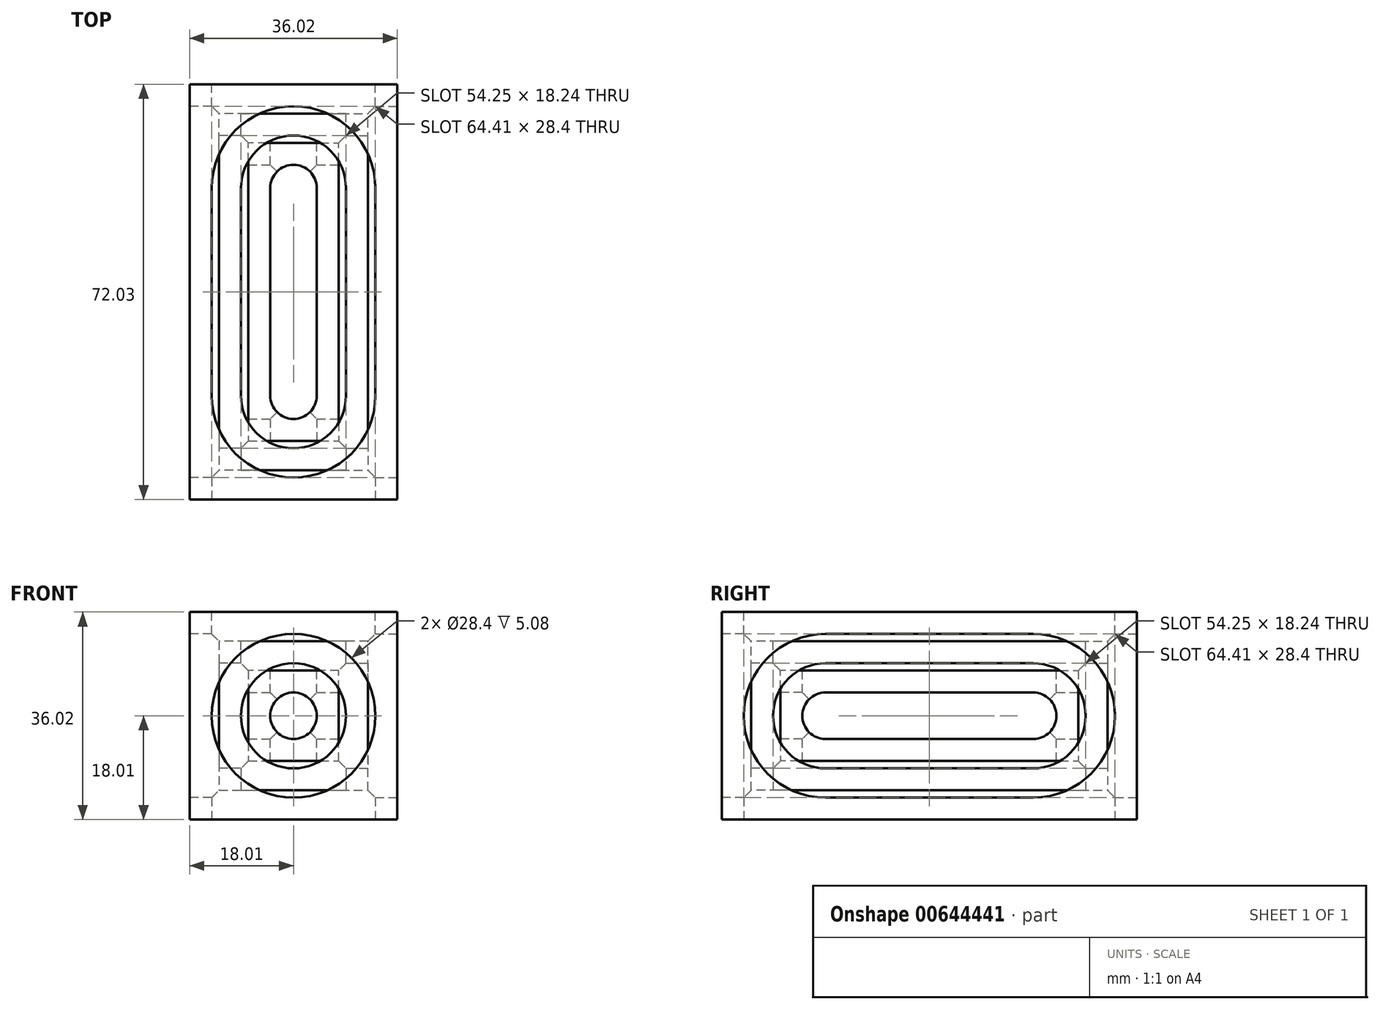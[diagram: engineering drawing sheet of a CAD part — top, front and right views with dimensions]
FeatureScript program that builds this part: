
annotation { "Feature Type Name" : "Feature", "Feature Type Description" : "" }
export const myFeature = defineFeature(function(context is Context, id is Id, definition is map)
    precondition{}
    {
        {
            var Q0;
            Q0=qCreatedBy(makeId("Front.planeOp"),FACE);
            var sketch = newSketch(context, id + "F0", { "sketchPlane" : qUnion([Q0])});
            skLineSegment(sketch, "E0.bottom", {"start": v(18, 18) * mm, "end": v(-18, 18) * mm});
            skLineSegment(sketch, "E0.top", {"start": v(18, -18) * mm, "end": v(-18, -18) * mm});
            skLineSegment(sketch, "E0.left", {"start": v(18, 18) * mm, "end": v(18, -18) * mm});
            skLineSegment(sketch, "E0.right", {"start": v(-18, 18) * mm, "end": v(-18, -18) * mm});
            skPoint(sketch, "E0.middle", {"position": v(0, 0) * mm});
            skSolve(sketch);
        }
        {
            var Q0;
            Q0 = qSketchRegion(id + "F0", true);
            extrude(context, id + "F1", {"entities" : qUnion([Q0]), "oppositeDirection" : true, "depth" : 72.03 * mm, "offsetDistance" : 25.4 * mm});
        }
        {
            var Q0;
            Q0=makeQuery(id+"F1.opExtrude","CAP_FACE",FACE,{"disambiguationData":[OSD([sQuery(id+"F0.wireOp",EDGE,"E0.bottom"),sQuery(id+"F0.wireOp",EDGE,"E0.top"),sQuery(id+"F0.wireOp",EDGE,"E0.left"),sQuery(id+"F0.wireOp",EDGE,"E0.right")])],"isStart":false});
            extrude(context, id + "F2", {"entities" : qUnion([Q0]), "depth" : 30.3 * mm, "offsetDistance" : 25.4 * mm});
        }
        {
            var Q0;
            Q0=makeQuery(id+"F1.opExtrude","SWEPT_FACE",FACE,{"disambiguationData":[OSD([sQuery(id+"F0.wireOp",EDGE,"E0.bottom")])]});
            var sketch = newSketch(context, id + "F3", { "sketchPlane" : qUnion([Q0])});
            skLineSegment(sketch, "E1", {"start": v(-18, 0) * mm, "end": v(-18, 36.02) * mm});
            skLineSegment(sketch, "E2", {"start": v(-18, 36.02) * mm, "end": v(-18, 72.03) * mm});
            skLineSegment(sketch, "E3", {"start": v(-18, 72.03) * mm, "end": v(0, 72.03) * mm});
            skLineSegment(sketch, "E4", {"start": v(0, 72.03) * mm, "end": v(0, 68.22) * mm});
            skLineSegment(sketch, "E5", {"start": v(-18, 0) * mm, "end": v(0, 0) * mm});
            skLineSegment(sketch, "E6", {"start": v(0, 0) * mm, "end": v(0, 3.81) * mm});
            skCircle(sketch, "E7", {"center": v(0, 18) * mm, "radius": 14.2 * mm});
            skPoint(sketch, "E7.centerSnap0", {"position": v(-18, 18) * mm});
            skCircle(sketch, "E8", {"center": v(0, 54.03) * mm, "radius": 14.2 * mm});
            skPoint(sketch, "E8.centerSnap0", {"position": v(-18, 54.03) * mm});
            skLineSegment(sketch, "E9", {"start": v(-14.2, 54.03) * mm, "end": v(-14.2, 18) * mm});
            skLineSegment(sketch, "E10", {"start": v(14.2, 54.03) * mm, "end": v(14.2, 18) * mm});
            skSolve(sketch);
        }
        {
            var Q0;
            {var subQ0=sQuery(id+"F3.wireOp",EDGE,"E7");var subQ1=makeQuery(id+"F3.imprint","INTERSECT",VERTEX,{"derivedFrom":[subQ0,sQuery(id+"F3.wireOp",EDGE,"E9")]});Q0=makeQuery(id+"F3.imprint","IMPRINT",FACE,{"disambiguationData":[TD([[makeQuery(id+"F3.imprint","IMPRINT",EDGE,{"disambiguationData":[TD([[subQ1,1.0]])],"derivedFrom":subQ0}),1.0]])]});}
            var Q1;
            {var subQ0=sQuery(id+"F3.wireOp",EDGE,"E8");var subQ1=makeQuery(id+"F3.imprint","INTERSECT",VERTEX,{"derivedFrom":[sQuery(id+"F3.wireOp",EDGE,"E4"),subQ0]});Q1=makeQuery(id+"F3.imprint","IMPRINT",FACE,{"disambiguationData":[TD([[makeQuery(id+"F3.imprint","IMPRINT",EDGE,{"disambiguationData":[TD([[subQ1,1.0]])],"derivedFrom":subQ0}),1.0]])]});}
            var Q2;
            {var subQ0=sQuery(id+"F3.wireOp",EDGE,"E9");Q2=makeQuery(id+"F3.imprint","IMPRINT",FACE,{"disambiguationData":[TD([[makeQuery(id+"F3.imprint","IMPRINT",EDGE,{"derivedFrom":subQ0}),1.0]])]});}
            extrude(context, id + "F4", {"entities" : qUnion([Q0, Q1, Q2]), "operationType" : NewBodyOperationType.REMOVE, "oppositeDirection" : true, "depth" : 5.08 * mm, "offsetDistance" : 25.4 * mm});
        }
        {
            var Q0;
            Q0=makeQuery(id+"F1.opExtrude","SWEPT_FACE",FACE,{"disambiguationData":[OSD([sQuery(id+"F0.wireOp",EDGE,"E0.left")])]});
            var sketch = newSketch(context, id + "F5", { "sketchPlane" : qUnion([Q0])});
            skLineSegment(sketch, "E11", {"start": v(0, 18) * mm, "end": v(36.02, 18) * mm});
            skLineSegment(sketch, "E12", {"start": v(36.02, 18) * mm, "end": v(72.03, 18) * mm});
            skLineSegment(sketch, "E13", {"start": v(72.03, 18) * mm, "end": v(72.03, 0) * mm});
            skLineSegment(sketch, "E14", {"start": v(72.03, 0) * mm, "end": v(68.22, 0) * mm});
            skLineSegment(sketch, "E15", {"start": v(0, 0) * mm, "end": v(3.81, 0) * mm});
            skCircle(sketch, "E16", {"center": v(18, 0) * mm, "radius": 14.2 * mm});
            skPoint(sketch, "E16.centerSnap0", {"position": v(18, 18) * mm});
            skCircle(sketch, "E17", {"center": v(54.03, 0) * mm, "radius": 14.2 * mm});
            skPoint(sketch, "E17.centerSnap0", {"position": v(54.03, 18) * mm});
            skLineSegment(sketch, "E18", {"start": v(18, 14.2) * mm, "end": v(54.03, 14.2) * mm});
            skLineSegment(sketch, "E19", {"start": v(18, -14.2) * mm, "end": v(54.03, -14.2) * mm});
            skSolve(sketch);
        }
        {
            var Q0;
            Q0 = qSketchRegion(id + "F5", true);
            extrude(context, id + "F6", {"entities" : qUnion([Q0]), "operationType" : NewBodyOperationType.REMOVE, "oppositeDirection" : true, "depth" : 5.08 * mm, "offsetDistance" : 25.4 * mm});
        }
        {
            var Q0;
            Q0=makeQuery(id+"F1.opExtrude","SWEPT_FACE",FACE,{"disambiguationData":[OSD([sQuery(id+"F0.wireOp",EDGE,"E0.top")])]});
            var sketch = newSketch(context, id + "F7", { "sketchPlane" : qUnion([Q0])});
            skLineSegment(sketch, "E20", {"start": v(18, 0) * mm, "end": v(18, -36.02) * mm});
            skLineSegment(sketch, "E21", {"start": v(18, -36.02) * mm, "end": v(18, -72.03) * mm});
            skLineSegment(sketch, "E22", {"start": v(18, -72.03) * mm, "end": v(0, -72.03) * mm});
            skLineSegment(sketch, "E23", {"start": v(0, -72.03) * mm, "end": v(0, -68.22) * mm});
            skLineSegment(sketch, "E24", {"start": v(0, 0) * mm, "end": v(0, -3.81) * mm});
            skCircle(sketch, "E25", {"center": v(0, -54.03) * mm, "radius": 14.2 * mm});
            skPoint(sketch, "E25.centerSnap0", {"position": v(18, -54.03) * mm});
            skCircle(sketch, "E26", {"center": v(0, -18) * mm, "radius": 14.2 * mm});
            skPoint(sketch, "E26.centerSnap0", {"position": v(18, -18) * mm});
            skLineSegment(sketch, "E27", {"start": v(-14.2, -18) * mm, "end": v(-14.2, -54.03) * mm});
            skLineSegment(sketch, "E28", {"start": v(14.2, -54.03) * mm, "end": v(14.2, -18) * mm});
            skSolve(sketch);
        }
        {
            var Q0;
            Q0 = qSketchRegion(id + "F7", true);
            extrude(context, id + "F8", {"entities" : qUnion([Q0]), "operationType" : NewBodyOperationType.REMOVE, "oppositeDirection" : true, "depth" : 5.08 * mm, "offsetDistance" : 25.4 * mm});
        }
        {
            var Q0;
            Q0=makeQuery(id+"F1.opExtrude","SWEPT_FACE",FACE,{"disambiguationData":[OSD([sQuery(id+"F0.wireOp",EDGE,"E0.right")])]});
            var sketch = newSketch(context, id + "F9", { "sketchPlane" : qUnion([Q0])});
            skLineSegment(sketch, "E29", {"start": v(0, 18) * mm, "end": v(-36.02, 18) * mm});
            skLineSegment(sketch, "E30", {"start": v(-36.02, 18) * mm, "end": v(-72.03, 18) * mm});
            skLineSegment(sketch, "E31", {"start": v(-72.03, 18) * mm, "end": v(-72.03, 0) * mm});
            skLineSegment(sketch, "E32", {"start": v(-72.03, 0) * mm, "end": v(-68.22, 0) * mm});
            skLineSegment(sketch, "E33", {"start": v(0, 0) * mm, "end": v(-3.81, 0) * mm});
            skCircle(sketch, "E34", {"center": v(-54.03, 0) * mm, "radius": 14.2 * mm});
            skPoint(sketch, "E34.centerSnap0", {"position": v(-54.03, 18) * mm});
            skCircle(sketch, "E35", {"center": v(-18, 0) * mm, "radius": 14.2 * mm});
            skPoint(sketch, "E35.centerSnap0", {"position": v(-18, 18) * mm});
            skLineSegment(sketch, "E36", {"start": v(-54.03, 14.2) * mm, "end": v(-18, 14.2) * mm});
            skLineSegment(sketch, "E37", {"start": v(-18, -14.2) * mm, "end": v(-54.03, -14.2) * mm});
            skSolve(sketch);
        }
        {
            var Q0;
            Q0 = qSketchRegion(id + "F9", true);
            extrude(context, id + "F10", {"entities" : qUnion([Q0]), "operationType" : NewBodyOperationType.REMOVE, "oppositeDirection" : true, "depth" : 5.08 * mm, "offsetDistance" : 25.4 * mm});
        }
        {
            var Q0;
            Q0=makeQuery(id+"F1.opExtrude","CAP_FACE",FACE,{"disambiguationData":[OSD([sQuery(id+"F0.wireOp",EDGE,"E0.bottom"),sQuery(id+"F0.wireOp",EDGE,"E0.top"),sQuery(id+"F0.wireOp",EDGE,"E0.left"),sQuery(id+"F0.wireOp",EDGE,"E0.right")])],"isStart":true});
            var sketch = newSketch(context, id + "F11", { "sketchPlane" : qUnion([Q0])});
            skLineSegment(sketch, "E38", {"start": v(-18, 0) * mm, "end": v(-18, 18) * mm});
            skLineSegment(sketch, "E39", {"start": v(-18, 18) * mm, "end": v(-18, 0) * mm});
            skLineSegment(sketch, "E40", {"start": v(-18, 0) * mm, "end": v(-14.2, 0) * mm});
            skCircle(sketch, "E41", {"center": v(0, 0) * mm, "radius": 14.2 * mm});
            skSolve(sketch);
        }
        {
            var Q0;
            Q0 = qSketchRegion(id + "F11", true);
            extrude(context, id + "F12", {"entities" : qUnion([Q0]), "operationType" : NewBodyOperationType.REMOVE, "oppositeDirection" : true, "depth" : 5.08 * mm, "offsetDistance" : 25.4 * mm});
        }
        {
            var Q0;
            Q0=makeQuery(id+"F12.boolean.opBoolean","COPY",FACE,{"derivedFrom":makeQuery(id+"F12.opExtrude","CAP_FACE",FACE,{"disambiguationData":[OSD([sQuery(id+"F11.wireOp",EDGE,"E41")])],"isStart":false})});
            var sketch = newSketch(context, id + "F13", { "sketchPlane" : qUnion([Q0])});
            skLineSegment(sketch, "E42", {"start": v(-5.87, 12.93) * mm, "end": v(0, 12.93) * mm});
            skLineSegment(sketch, "E43", {"start": v(0, 12.93) * mm, "end": v(0, 9.12) * mm});
            skCircle(sketch, "E44", {"center": v(0, 0) * mm, "radius": 9.12 * mm});
            skSolve(sketch);
        }
        {
            var Q0;
            Q0 = qSketchRegion(id + "F13", true);
            extrude(context, id + "F14", {"entities" : qUnion([Q0]), "operationType" : NewBodyOperationType.REMOVE, "oppositeDirection" : true, "depth" : 5.08 * mm, "offsetDistance" : 25.4 * mm});
        }
        {
            var Q0;
            Q0=makeQuery(id+"F1.opExtrude","CAP_FACE",FACE,{"disambiguationData":[OSD([sQuery(id+"F0.wireOp",EDGE,"E0.bottom"),sQuery(id+"F0.wireOp",EDGE,"E0.top"),sQuery(id+"F0.wireOp",EDGE,"E0.left"),sQuery(id+"F0.wireOp",EDGE,"E0.right")])],"isStart":false});
            var sketch = newSketch(context, id + "F15", { "sketchPlane" : qUnion([Q0])});
            skLineSegment(sketch, "E45", {"start": v(0, 18) * mm, "end": v(0, 14.2) * mm});
            skPoint(sketch, "E45.endSnap0", {"position": v(0, 18) * mm});
            skCircle(sketch, "E46", {"center": v(0, 0) * mm, "radius": 14.2 * mm});
            skSolve(sketch);
        }
        {
            var Q0;
            Q0 = qSketchRegion(id + "F15", true);
            extrude(context, id + "F16", {"entities" : qUnion([Q0]), "operationType" : NewBodyOperationType.REMOVE, "oppositeDirection" : true, "depth" : 5.08 * mm, "offsetDistance" : 25.4 * mm});
        }
        {
            var Q0;
            Q0=makeQuery(id+"F6.boolean.opBoolean","COPY",FACE,{"derivedFrom":makeQuery(id+"F6.opExtrude","CAP_FACE",FACE,{"disambiguationData":[OSD([sQuery(id+"F5.wireOp",EDGE,"E16"),sQuery(id+"F5.wireOp",EDGE,"E17"),sQuery(id+"F5.wireOp",EDGE,"E18"),sQuery(id+"F5.wireOp",EDGE,"E19")])],"isStart":false})});
            var sketch = newSketch(context, id + "F17", { "sketchPlane" : qUnion([Q0])});
            skLineSegment(sketch, "E47", {"start": v(5.08, 0) * mm, "end": v(8.9, 0) * mm});
            skPoint(sketch, "E47.endSnap0", {"position": v(5.08, 0) * mm});
            skLineSegment(sketch, "E48", {"start": v(66.95, 0) * mm, "end": v(63.14, 0) * mm});
            skCircle(sketch, "E49", {"center": v(18, 0) * mm, "radius": 9.12 * mm});
            skCircle(sketch, "E50", {"center": v(54.03, 0) * mm, "radius": 9.12 * mm});
            skLineSegment(sketch, "E51", {"start": v(18, 9.12) * mm, "end": v(54.03, 9.12) * mm});
            skLineSegment(sketch, "E52", {"start": v(18, -9.12) * mm, "end": v(54.03, -9.12) * mm});
            skSolve(sketch);
        }
        {
            var Q0;
            Q0 = qSketchRegion(id + "F17", true);
            extrude(context, id + "F18", {"entities" : qUnion([Q0]), "operationType" : NewBodyOperationType.REMOVE, "oppositeDirection" : true, "depth" : 5.08 * mm, "offsetDistance" : 25.4 * mm});
        }
        {
            var Q0;
            Q0=makeQuery(id+"F4.boolean.opBoolean","COPY",FACE,{"derivedFrom":makeQuery(id+"F4.opExtrude","CAP_FACE",FACE,{"disambiguationData":[OSD([sQuery(id+"F3.wireOp",EDGE,"E7"),sQuery(id+"F3.wireOp",EDGE,"E8"),sQuery(id+"F3.wireOp",EDGE,"E9"),sQuery(id+"F3.wireOp",EDGE,"E10")])],"isStart":false})});
            var sketch = newSketch(context, id + "F19", { "sketchPlane" : qUnion([Q0])});
            skLineSegment(sketch, "E53", {"start": v(0, 5.08) * mm, "end": v(0, 8.9) * mm});
            skPoint(sketch, "E53.endSnap0", {"position": v(0, 5.08) * mm});
            skLineSegment(sketch, "E54", {"start": v(0, 66.95) * mm, "end": v(0, 63.14) * mm});
            skPoint(sketch, "E54.endSnap0", {"position": v(0, 66.95) * mm});
            skCircle(sketch, "E55", {"center": v(0, 54.03) * mm, "radius": 9.12 * mm});
            skCircle(sketch, "E56", {"center": v(0, 18) * mm, "radius": 9.12 * mm});
            skLineSegment(sketch, "E57", {"start": v(-9.12, 54.03) * mm, "end": v(-9.12, 18) * mm});
            skLineSegment(sketch, "E58", {"start": v(9.12, 54.03) * mm, "end": v(9.12, 18) * mm});
            skSolve(sketch);
        }
        {
            var Q0;
            Q0 = qSketchRegion(id + "F19", true);
            extrude(context, id + "F20", {"entities" : qUnion([Q0]), "operationType" : NewBodyOperationType.REMOVE, "oppositeDirection" : true, "depth" : 5.08 * mm, "offsetDistance" : 25.4 * mm});
        }
        {
            var Q0;
            Q0=makeQuery(id+"F10.boolean.opBoolean","COPY",FACE,{"derivedFrom":makeQuery(id+"F10.opExtrude","CAP_FACE",FACE,{"disambiguationData":[OSD([sQuery(id+"F9.wireOp",EDGE,"E34"),sQuery(id+"F9.wireOp",EDGE,"E35"),sQuery(id+"F9.wireOp",EDGE,"E36"),sQuery(id+"F9.wireOp",EDGE,"E37")])],"isStart":false})});
            var sketch = newSketch(context, id + "F21", { "sketchPlane" : qUnion([Q0])});
            skLineSegment(sketch, "E59", {"start": v(-66.95, 0) * mm, "end": v(-63.14, 0) * mm});
            skPoint(sketch, "E59.endSnap0", {"position": v(-66.95, 0) * mm});
            skLineSegment(sketch, "E60", {"start": v(-5.08, 0) * mm, "end": v(-8.9, 0) * mm});
            skPoint(sketch, "E60.endSnap0", {"position": v(-5.08, 0) * mm});
            skCircle(sketch, "E61", {"center": v(-54.03, 0) * mm, "radius": 9.12 * mm});
            skCircle(sketch, "E62", {"center": v(-18, 0) * mm, "radius": 9.12 * mm});
            skLineSegment(sketch, "E63", {"start": v(-54.03, 9.12) * mm, "end": v(-18, 9.12) * mm});
            skLineSegment(sketch, "E64", {"start": v(-18, -9.12) * mm, "end": v(-54.03, -9.12) * mm});
            skSolve(sketch);
        }
        {
            var Q0;
            Q0 = qSketchRegion(id + "F21", true);
            extrude(context, id + "F22", {"entities" : qUnion([Q0]), "operationType" : NewBodyOperationType.REMOVE, "oppositeDirection" : true, "depth" : 5.08 * mm, "offsetDistance" : 25.4 * mm});
        }
        {
            var Q0;
            Q0=makeQuery(id+"F8.boolean.opBoolean","COPY",FACE,{"derivedFrom":makeQuery(id+"F8.opExtrude","CAP_FACE",FACE,{"disambiguationData":[OSD([sQuery(id+"F7.wireOp",EDGE,"E25"),sQuery(id+"F7.wireOp",EDGE,"E26"),sQuery(id+"F7.wireOp",EDGE,"E27"),sQuery(id+"F7.wireOp",EDGE,"E28")])],"isStart":false})});
            var sketch = newSketch(context, id + "F23", { "sketchPlane" : qUnion([Q0])});
            skLineSegment(sketch, "E65", {"start": v(0, -5.08) * mm, "end": v(0, -8.9) * mm});
            skPoint(sketch, "E65.endSnap0", {"position": v(0, -5.08) * mm});
            skLineSegment(sketch, "E66", {"start": v(0, -66.95) * mm, "end": v(0, -63.14) * mm});
            skCircle(sketch, "E67", {"center": v(0, -54.03) * mm, "radius": 9.12 * mm});
            skCircle(sketch, "E68", {"center": v(0, -18) * mm, "radius": 9.12 * mm});
            skLineSegment(sketch, "E69", {"start": v(-9.12, -18) * mm, "end": v(-9.12, -54.03) * mm});
            skLineSegment(sketch, "E70", {"start": v(9.12, -54.03) * mm, "end": v(9.12, -18) * mm});
            skSolve(sketch);
        }
        {
            var Q0;
            Q0 = qSketchRegion(id + "F23", true);
            extrude(context, id + "F24", {"entities" : qUnion([Q0]), "operationType" : NewBodyOperationType.REMOVE, "oppositeDirection" : true, "depth" : 5.08 * mm, "offsetDistance" : 25.4 * mm});
        }
        {
            var Q0;
            Q0=makeQuery(id+"F16.boolean.opBoolean","COPY",FACE,{"derivedFrom":makeQuery(id+"F16.opExtrude","CAP_FACE",FACE,{"disambiguationData":[OSD([sQuery(id+"F15.wireOp",EDGE,"E46")])],"isStart":false})});
            var sketch = newSketch(context, id + "F25", { "sketchPlane" : qUnion([Q0])});
            skLineSegment(sketch, "E71", {"start": v(0, 12.93) * mm, "end": v(0, 9.12) * mm});
            skCircle(sketch, "E72", {"center": v(0, 0) * mm, "radius": 9.12 * mm});
            skSolve(sketch);
        }
        {
            var Q0;
            Q0 = qSketchRegion(id + "F25", true);
            extrude(context, id + "F26", {"entities" : qUnion([Q0]), "operationType" : NewBodyOperationType.REMOVE, "oppositeDirection" : true, "depth" : 5.08 * mm, "offsetDistance" : 25.4 * mm});
        }
        {
            var Q0;
            Q0=makeQuery(id+"F20.boolean.opBoolean","COPY",FACE,{"derivedFrom":makeQuery(id+"F20.opExtrude","CAP_FACE",FACE,{"disambiguationData":[OSD([sQuery(id+"F19.wireOp",EDGE,"E55"),sQuery(id+"F19.wireOp",EDGE,"E56"),sQuery(id+"F19.wireOp",EDGE,"E57"),sQuery(id+"F19.wireOp",EDGE,"E58")])],"isStart":false})});
            var sketch = newSketch(context, id + "F27", { "sketchPlane" : qUnion([Q0])});
            skLineSegment(sketch, "E73", {"start": v(-4.64, 61.87) * mm, "end": v(0, 61.87) * mm});
            skLineSegment(sketch, "E74", {"start": v(0, 61.87) * mm, "end": v(0, 58.06) * mm});
            skLineSegment(sketch, "E75", {"start": v(0, 10.16) * mm, "end": v(0, 13.97) * mm});
            skCircle(sketch, "E76", {"center": v(0, 18) * mm, "radius": 4.04 * mm});
            skCircle(sketch, "E77", {"center": v(0, 54.03) * mm, "radius": 4.04 * mm});
            skLineSegment(sketch, "E78", {"start": v(-4.04, 54.03) * mm, "end": v(-4.04, 18) * mm});
            skLineSegment(sketch, "E79", {"start": v(4.04, 18) * mm, "end": v(4.04, 54.03) * mm});
            skSolve(sketch);
        }
        {
            var Q0;
            Q0 = qSketchRegion(id + "F27", true);
            extrude(context, id + "F28", {"entities" : qUnion([Q0]), "operationType" : NewBodyOperationType.REMOVE, "oppositeDirection" : true, "depth" : 17.78 * mm, "offsetDistance" : 25.4 * mm});
        }
        {
            var Q0;
            Q0=makeQuery(id+"F18.boolean.opBoolean","COPY",FACE,{"derivedFrom":makeQuery(id+"F18.opExtrude","CAP_FACE",FACE,{"disambiguationData":[OSD([sQuery(id+"F17.wireOp",EDGE,"E49"),sQuery(id+"F17.wireOp",EDGE,"E50"),sQuery(id+"F17.wireOp",EDGE,"E51"),sQuery(id+"F17.wireOp",EDGE,"E52")])],"isStart":false})});
            var sketch = newSketch(context, id + "F29", { "sketchPlane" : qUnion([Q0])});
            skLineSegment(sketch, "E80", {"start": v(10.16, 0) * mm, "end": v(13.97, 0) * mm});
            skLineSegment(sketch, "E81", {"start": v(61.87, 0) * mm, "end": v(58.06, 0) * mm});
            skCircle(sketch, "E82", {"center": v(18, 0) * mm, "radius": 4.04 * mm});
            skCircle(sketch, "E83", {"center": v(54.03, 0) * mm, "radius": 4.04 * mm});
            skLineSegment(sketch, "E84", {"start": v(18, 4.04) * mm, "end": v(54.03, 4.04) * mm});
            skLineSegment(sketch, "E85", {"start": v(54.03, -4.04) * mm, "end": v(18, -4.04) * mm});
            skSolve(sketch);
        }
        {
            var Q0;
            Q0 = qSketchRegion(id + "F29", true);
            extrude(context, id + "F30", {"entities" : qUnion([Q0]), "operationType" : NewBodyOperationType.REMOVE, "oppositeDirection" : true, "depth" : 17.78 * mm, "offsetDistance" : 25.4 * mm});
        }
        {
            var Q0;
            Q0=makeQuery(id+"F26.boolean.opBoolean","COPY",FACE,{"derivedFrom":makeQuery(id+"F26.opExtrude","CAP_FACE",FACE,{"disambiguationData":[OSD([sQuery(id+"F25.wireOp",EDGE,"E72")])],"isStart":false})});
            var sketch = newSketch(context, id + "F31", { "sketchPlane" : qUnion([Q0])});
            skLineSegment(sketch, "E86", {"start": v(0, 7.85) * mm, "end": v(0, 4.04) * mm});
            skCircle(sketch, "E87", {"center": v(0, 0) * mm, "radius": 4.04 * mm});
            skSolve(sketch);
        }
        {
            var Q0;
            Q0 = qSketchRegion(id + "F31", true);
            extrude(context, id + "F32", {"entities" : qUnion([Q0]), "operationType" : NewBodyOperationType.REMOVE, "oppositeDirection" : true, "depth" : 5.08 * mm, "offsetDistance" : 25.4 * mm});
        }
        {
            var Q0;
            Q0=makeQuery(id+"F14.boolean.opBoolean","COPY",FACE,{"derivedFrom":makeQuery(id+"F14.opExtrude","CAP_FACE",FACE,{"disambiguationData":[OSD([sQuery(id+"F13.wireOp",EDGE,"E44")])],"isStart":false})});
            var sketch = newSketch(context, id + "F33", { "sketchPlane" : qUnion([Q0])});
            skLineSegment(sketch, "E88", {"start": v(0, 7.85) * mm, "end": v(0, 4.04) * mm});
            skCircle(sketch, "E89", {"center": v(0, 0) * mm, "radius": 4.04 * mm});
            skSolve(sketch);
        }
        {
            var Q0;
            Q0 = qSketchRegion(id + "F33", true);
            extrude(context, id + "F34", {"entities" : qUnion([Q0]), "operationType" : NewBodyOperationType.REMOVE, "oppositeDirection" : true, "depth" : 5.08 * mm, "offsetDistance" : 25.4 * mm});
        }
        {
            var Q0;
            Q0=makeQuery(id+"F2.opExtrude","SWEPT_BODY",BODY,{"disambiguationData":[OSD([sQuery(id+"F0.wireOp",EDGE,"E0.bottom"),sQuery(id+"F0.wireOp",EDGE,"E0.top"),sQuery(id+"F0.wireOp",EDGE,"E0.left"),sQuery(id+"F0.wireOp",EDGE,"E0.right")])]});
            deleteBodies(context, id + "F35", {"entities" : qUnion([Q0])});
        }
    });
